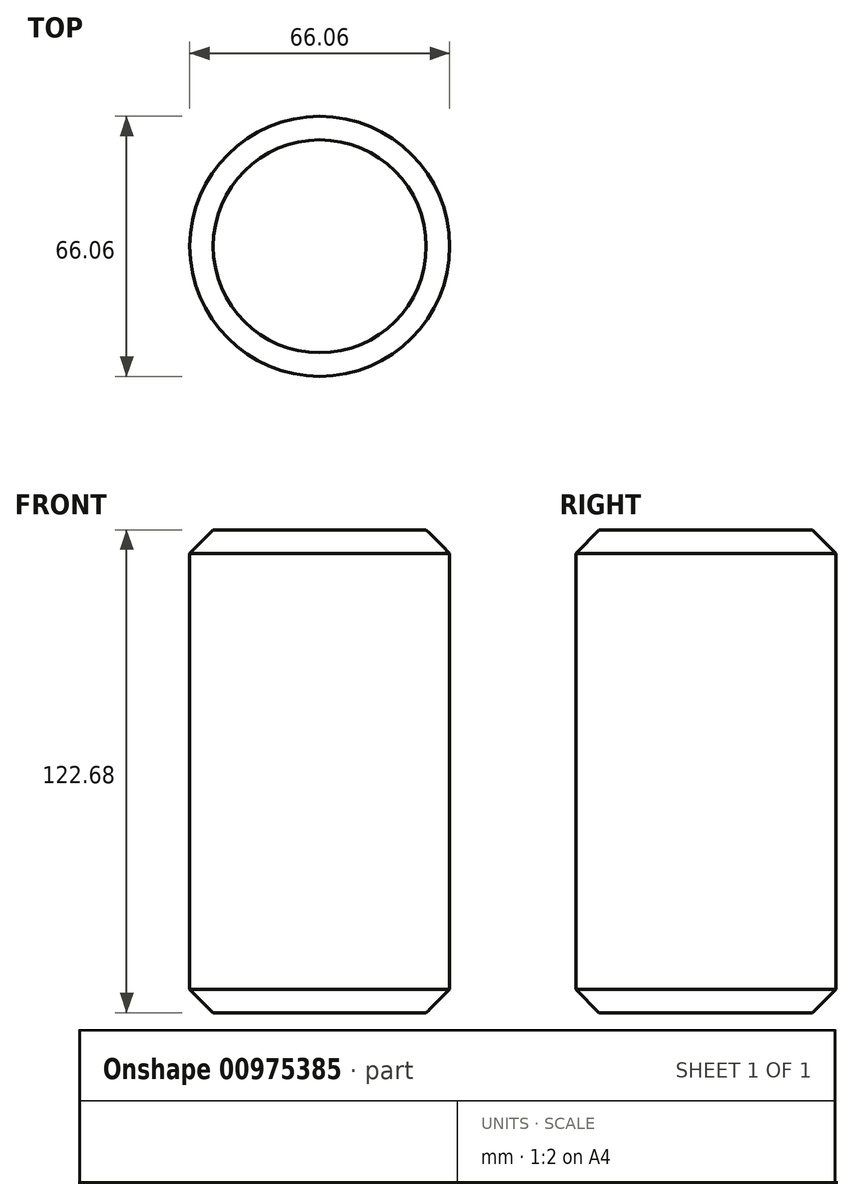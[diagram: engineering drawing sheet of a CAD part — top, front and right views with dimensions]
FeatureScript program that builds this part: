
annotation { "Feature Type Name" : "Feature", "Feature Type Description" : "" }
export const myFeature = defineFeature(function(context is Context, id is Id, definition is map)
    precondition{}
    {
        {
            var Q0;
            Q0=qCreatedBy(makeId("Front.planeOp"),FACE);
            var sketch = newSketch(context, id + "F0", { "sketchPlane" : qUnion([Q0])});
            skLineSegment(sketch, "E0.bottom", {"start": v(-27.05, 61.34) * mm, "end": v(0, 61.34) * mm});
            skLineSegment(sketch, "E0.top", {"start": v(-27.05, -61.34) * mm, "end": v(0, -61.34) * mm});
            skLineSegment(sketch, "E0.left", {"start": v(-33.02, 55.37) * mm, "end": v(-33.02, -55.37) * mm});
            skPoint(sketch, "E0.middle", {"position": v(0, 0) * mm});
            skPoint(sketch, "E1", {"position": v(-27.05, 61.34) * mm});
            skLineSegment(sketch, "E2", {"start": v(-27.05, 61.34) * mm, "end": v(-33.03, 55.37) * mm});
            skPoint(sketch, "E3.orphan", {"position": v(-33.02, 61.34) * mm});
            skLineSegment(sketch, "E4", {"start": v(0, 61.34) * mm, "end": v(0, -61.34) * mm, "construction": true});
            skLineSegment(sketch, "E5", {"start": v(0, 61.34) * mm, "end": v(0, -61.34) * mm});
            skPoint(sketch, "E0.right.end.orphan", {"position": v(33.03, -61.34) * mm});
            skPoint(sketch, "E6.orphan", {"position": v(33.03, 61.34) * mm});
            skLineSegment(sketch, "E7.MirrorCS", {"start": v(-27.05, -61.34) * mm, "end": v(-33.02, -55.37) * mm});
            skPoint(sketch, "E8.orphan", {"position": v(-33.02, -61.34) * mm});
            skSolve(sketch);
        }
        {
            var Q0;
            Q0=makeQuery(id+"F0.imprint","IMPRINT",FACE,{"disambiguationData":[TD([[makeQuery(id+"F0.imprint","IMPRINT",EDGE,{"derivedFrom":sQuery(id+"F0.wireOp",EDGE,"E0.bottom")}),-1.0]])]});
            var Q1;
            Q1=sQuery(id+"F0.wireOp",EDGE,"E4");
            revolve(context, id + "F1", {"surfaceOperationType" : NewSurfaceOperationType.NEW, "entities" : qUnion([Q0]), "axis" : qUnion([Q1]), "revolveType" : RevolveType.FULL});
        }
    });
